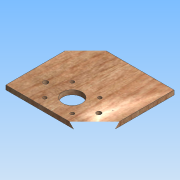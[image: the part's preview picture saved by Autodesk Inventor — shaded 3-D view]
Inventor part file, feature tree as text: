
AUTODESK INVENTOR PART (.ipt)
format: ipt  version: 2015 (Build 190159000, 159)  size: 268,288 bytes
history: native  units: mm
features: sketch x10, other x9, extrude x4, hole x3, projected_geometry x1
ambient origin geometry x8: Origin, YZ Plane, XZ Plane, XY Plane, X Axis, Y Axis, Z Axis, Center Point
bodies: Body1 (feature_tree)
feature tree (27):
  other  "Blocks"
  extrude  "Extrusion2"  Depth=100.0mm
  hole  "Hole4"  [1 undecoded]
  hole  "Hole5"  [1 undecoded]
  hole  "Hole8"  [1 undecoded]
  extrude  "Extrusion5"  Depth=20.0mm
  extrude  "Extrusion6"  TaperAngle=0.0deg  [1 undecoded]
  extrude  "Extrusion10"  Depth=10.0mm
  sketch  "Sketch42"  dims[d129=5.5mm d130=0.0mm]
  sketch  "Sketch43"  dims[d131=5.5mm d132=10.0mm]
  sketch  "Sketch41"  dims[d122=5.5mm d123=20.0mm]
  sketch  "Sketch10"  dims[d21=100.0mm d22=50.0mm]
  sketch  "Sketch13"  dims[d23=5.0mm d24=0.0mm d43=31.0mm]
  sketch  "Sketch16"  dims[d44=31.0mm]
  sketch  "Sketch17"  dims[d45=4.0mm d46=6.0mm d47=4.0mm d48=2.0mm d49=90.0deg d50=4.0mm d51=0.0mm d52=60.0mm]
  sketch  "Sketch33"  dims[d53=5.2mm d54=6.0mm d55=4.0mm d56=2.0mm d57=90.0deg d58=4.0mm d59=0.0mm]
  sketch  "Sketch34"  dims[d78=22.0mm d79=6.0mm d80=4.0mm d81=2.0mm d82=90.0deg d83=2.0mm d84=0.0mm d121=20.0mm]
  other  "Block1"
  other  "Block2"
  other  "Block3"
  other  "Block4"
  sketch  "Sketch45"  dims[d133=8.333333mm d134=5.5mm d135=0.0mm d189=40.0mm d190=5.0mm d191=0.0mm d29=1.0mm d30=1.0mm]
  projected_geometry  "Projected Loop4"
  other  "Block3:1"
  other  "Block3:2"
  other  "Block4:1"
  other  "Block4:2"
note: 4 required parameter values undecoded (feature->parameter linkage not recoverable at this tier; creation-order binding heuristic only, values carry confidence <= 0.55)
